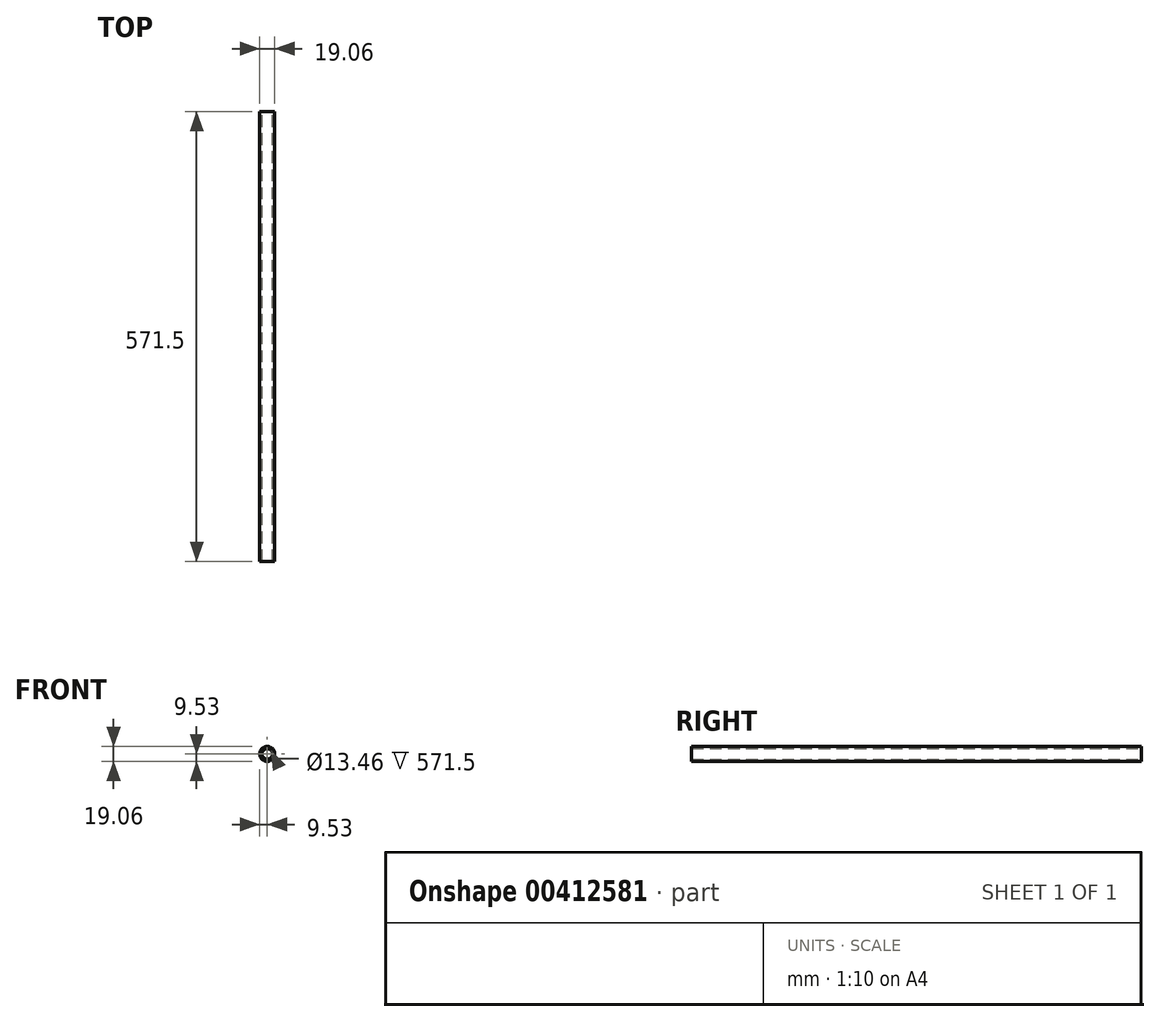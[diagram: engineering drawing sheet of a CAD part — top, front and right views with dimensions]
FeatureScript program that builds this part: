
annotation { "Feature Type Name" : "Feature", "Feature Type Description" : "" }
export const myFeature = defineFeature(function(context is Context, id is Id, definition is map)
    precondition{}
    {
        {
            var Q0;
            Q0=qCreatedBy(makeId("Front.planeOp"),FACE);
            var sketch = newSketch(context, id + "F0", { "sketchPlane" : qUnion([Q0])});
            skCircle(sketch, "E0", {"center": v(0, 0) * mm, "radius": 9.53 * mm});
            skCircle(sketch, "E1", {"center": v(0, 0) * mm, "radius": 6.73 * mm});
            skSolve(sketch);
        }
        {
            var Q0;
            Q0=makeQuery(id+"F0.imprint","IMPRINT",FACE,{"disambiguationData":[TD([[makeQuery(id+"F0.imprint","IMPRINT",EDGE,{"derivedFrom":sQuery(id+"F0.wireOp",EDGE,"E0")}),1.0]])]});
            extrude(context, id + "F1", {"entities" : qUnion([Q0]), "depth" : 571.5 * mm});
        }
    });
